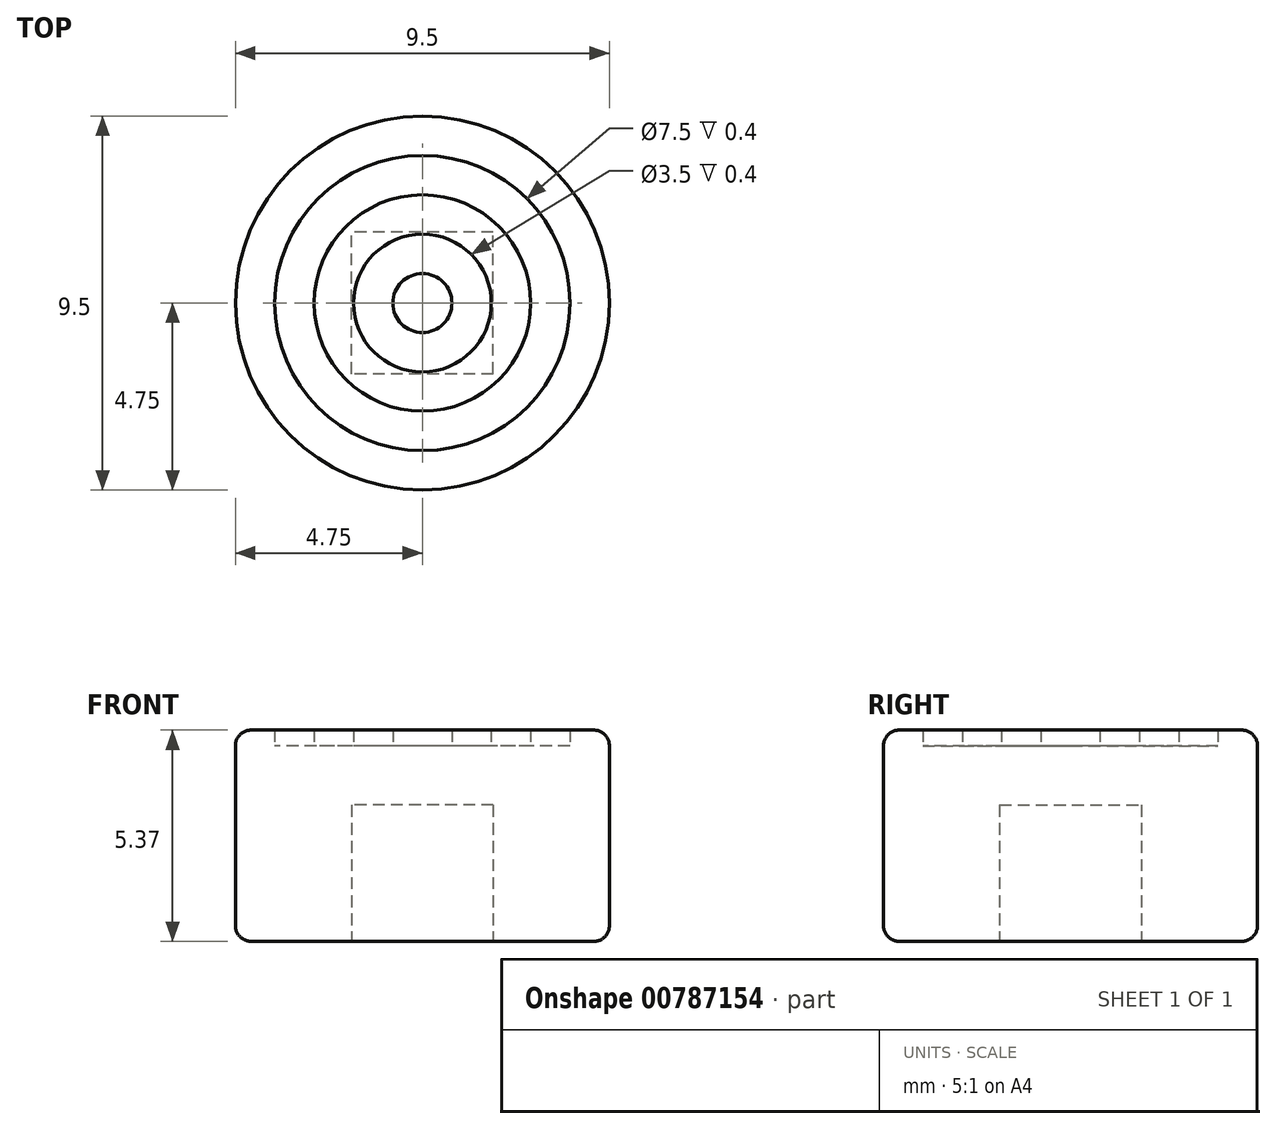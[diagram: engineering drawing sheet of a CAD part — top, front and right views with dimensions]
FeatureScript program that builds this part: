
annotation { "Feature Type Name" : "Feature", "Feature Type Description" : "" }
export const myFeature = defineFeature(function(context is Context, id is Id, definition is map)
    precondition{}
    {
        {
            var Q0;
            Q0=qCreatedBy(makeId("Top.planeOp"),FACE);
            var sketch = newSketch(context, id + "F0", { "sketchPlane" : qUnion([Q0])});
            skLineSegment(sketch, "E0.bottom", {"start": v(1.8, -1.8) * mm, "end": v(-1.8, -1.8) * mm});
            skLineSegment(sketch, "E0.top", {"start": v(1.8, 1.8) * mm, "end": v(-1.8, 1.8) * mm});
            skLineSegment(sketch, "E0.left", {"start": v(1.8, -1.8) * mm, "end": v(1.8, 1.8) * mm});
            skLineSegment(sketch, "E0.right", {"start": v(-1.8, -1.8) * mm, "end": v(-1.8, 1.8) * mm});
            skPoint(sketch, "E0.middle", {"position": v(0, 0) * mm});
            skCircle(sketch, "E1", {"center": v(0, 0) * mm, "radius": 4.75 * mm});
            skSolve(sketch);
        }
        {
            var Q0;
            Q0=makeQuery(id+"F0.imprint","IMPRINT",FACE,{"disambiguationData":[TD([[makeQuery(id+"F0.imprint","IMPRINT",EDGE,{"derivedFrom":sQuery(id+"F0.wireOp",EDGE,"E0.bottom")}),1.0]])]});
            extrude(context, id + "F1", {"entities" : qUnion([Q0]), "depth" : 3.47 * mm});
        }
        {
            var Q0;
            Q0=makeQuery(id+"F1.opExtrude","CAP_FACE",FACE,{"disambiguationData":[OSD([sQuery(id+"F0.wireOp",EDGE,"E0.bottom"),sQuery(id+"F0.wireOp",EDGE,"E0.top"),sQuery(id+"F0.wireOp",EDGE,"E0.left"),sQuery(id+"F0.wireOp",EDGE,"E0.right"),sQuery(id+"F0.wireOp",EDGE,"E1")])],"isStart":false});
            var sketch = newSketch(context, id + "F2", { "sketchPlane" : qUnion([Q0])});
            skSolve(sketch);
        }
        {
            var Q0;
            Q0=qSketchRegion(id+"F2",true);
            var Q1;
            Q1=makeQuery(id+"F2.imprint","IMPRINT",FACE,{"disambiguationData":[TD([[makeQuery(id+"F2.imprint","IMPRINT",EDGE,{"derivedFrom":makeQuery(id+"F1.opExtrude","CAP_EDGE",EDGE,{"disambiguationData":[OSD([sQuery(id+"F0.wireOp",EDGE,"E0.bottom")])],"isStart":false})}),1.0]])]});
            var Q2;
            Q2=makeQuery(id+"F2.imprint","IMPRINT",FACE,{"disambiguationData":[TD([[makeQuery(id+"F2.imprint","IMPRINT",EDGE,{"derivedFrom":makeQuery(id+"F1.opExtrude","CAP_EDGE",EDGE,{"disambiguationData":[OSD([sQuery(id+"F0.wireOp",EDGE,"E0.bottom")])],"isStart":false})}),-1.0]])]});
            extrude(context, id + "F3", {"entities" : qUnion([Q0, Q1, Q2]), "operationType" : NewBodyOperationType.ADD, "depth" : 1.5 * mm});
        }
        {
            var Q0;
            Q0=makeQuery(id+"F3.opExtrude","CAP_FACE",FACE,{"disambiguationData":[OSD([sQuery(id+"F0.wireOp",EDGE,"E1")])],"isStart":false});
            var sketch = newSketch(context, id + "F4", { "sketchPlane" : qUnion([Q0])});
            skCircle(sketch, "E2", {"center": v(0, 0) * mm, "radius": 3.75 * mm});
            skCircle(sketch, "E3", {"center": v(0, 0) * mm, "radius": 2.75 * mm});
            skCircle(sketch, "E4", {"center": v(0, 0) * mm, "radius": 1.75 * mm});
            skCircle(sketch, "E5", {"center": v(0, 0) * mm, "radius": 0.75 * mm});
            skSolve(sketch);
        }
        {
            var Q0;
            Q0=makeQuery(id+"F4.imprint","IMPRINT",FACE,{"disambiguationData":[TD([[makeQuery(id+"F4.imprint","IMPRINT",EDGE,{"derivedFrom":sQuery(id+"F4.wireOp",EDGE,"E2")}),-1.0]])]});
            var Q1;
            Q1=makeQuery(id+"F4.imprint","IMPRINT",FACE,{"disambiguationData":[TD([[makeQuery(id+"F4.imprint","IMPRINT",EDGE,{"derivedFrom":sQuery(id+"F4.wireOp",EDGE,"E3")}),1.0]])]});
            var Q2;
            Q2=makeQuery(id+"F4.imprint","IMPRINT",FACE,{"disambiguationData":[TD([[makeQuery(id+"F4.imprint","IMPRINT",EDGE,{"derivedFrom":sQuery(id+"F4.wireOp",EDGE,"E5")}),1.0]])]});
            extrude(context, id + "F5", {"entities" : qUnion([Q0, Q1, Q2]), "operationType" : NewBodyOperationType.ADD, "depth" : .4 * mm});
        }
        {
            var Q0;
            Q0=makeQuery(id+"F5.opExtrude","CAP_EDGE",EDGE,{"disambiguationData":[OSD([sQuery(id+"F0.wireOp",EDGE,"E1")])],"isStart":false});
            var Q1;
            Q1=makeQuery(id+"F1.opExtrude","CAP_EDGE",EDGE,{"disambiguationData":[OSD([sQuery(id+"F0.wireOp",EDGE,"E1")])],"isStart":true});
            fillet(context, id + "F6", {"entities" : qUnion([Q0, Q1]), "radius" : 0.4 * mm, "tangentPropagation" : true, "allowEdgeOverflow" : false});
        }
    });
